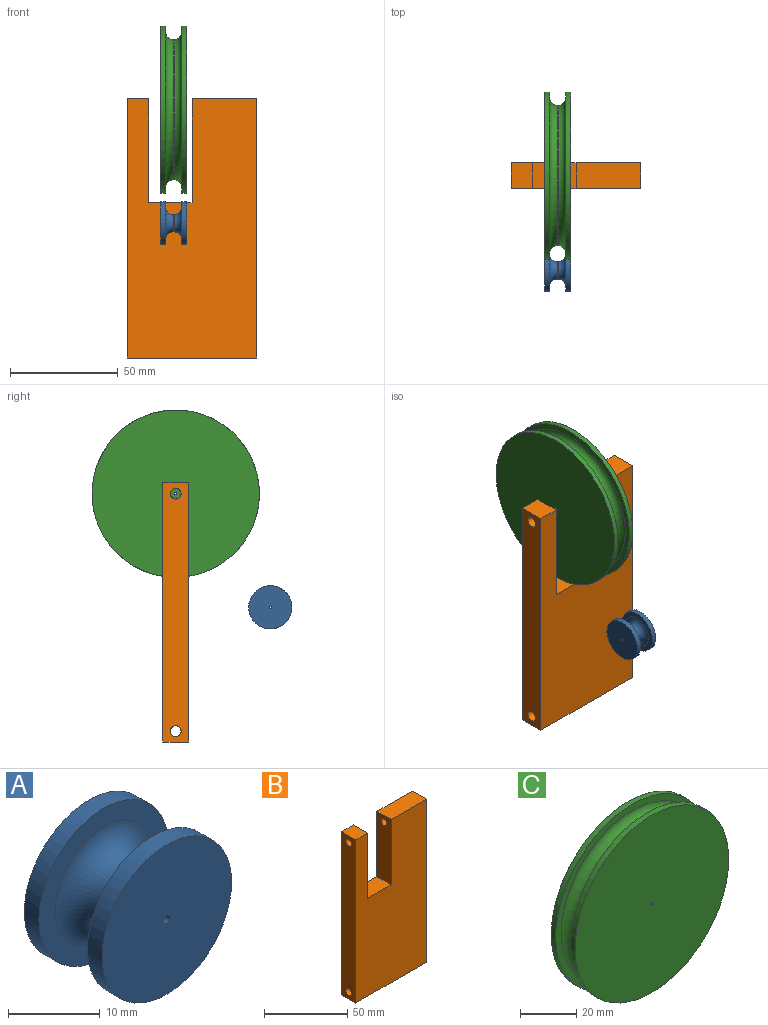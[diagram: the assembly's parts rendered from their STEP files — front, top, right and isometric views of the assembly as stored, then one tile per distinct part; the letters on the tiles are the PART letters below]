
ASSEMBLY  parts=3 mates=3
PART A: 10 faces, bbox 21.6x12x21.6 mm
  f0: cylinder r=10mm len=20mm, axis (0,1,0), area 141.4mm2, adj f1,f5
  f1: plane 20x20mm, normal (0,1,0), area 313.4mm2, adj f0,f9
  f2: torus R=7.5mm, axis (0,-1,0), area 182.1mm2, adj f3,f6
  f3: cylinder r=4mm len=8mm, axis (0,-1,0), area 12.6mm2, adj f2,f4
  f4: torus R=7.5mm, axis (0,-1,0), area 182.1mm2, adj f3,f5
  f5: plane 20x20mm, normal (0,-1,0), area 137.4mm2, adj f0,f4
  f6: plane 20x20mm, normal (0,1,0), area 137.4mm2, adj f2,f8
  f7: plane 20x20mm, normal (0,-1,0), area 313.4mm2, adj f8,f9
  f8: cylinder r=10mm len=20mm, axis (0,1,0), area 141.4mm2, adj f6,f7
  f9: cylinder r=0.5mm len=12mm, axis (0,1,0), area 37.7mm2, adj f1,f7
PART B: 13 faces, bbox 60x12x120 mm
  f0: plane 30x12mm, normal (0,0,1), area 360mm2, adj f1,f2,f3,f7
  f1: plane 120x60mm, normal (0,-1,0), area 6240mm2, adj f0,f3,f4,f5,f6,f7,f8,f9
  f2: plane 120x60mm, normal (0,1,0), area 6240mm2, adj f0,f3,f4,f5,f6,f7,f8,f9
  f3: plane 120x12mm, normal (1,0,0), area 1400.7mm2, adj f0,f1,f2,f6,f11,f12
  f4: plane 12x10mm, normal (0,0,1), area 120mm2, adj f1,f2,f5,f9
  f5: plane 120x12mm, normal (-1,0,0), area 1400.7mm2, adj f1,f2,f4,f6,f10,f12
  f6: plane 60x12mm, normal (0,0,-1), area 720mm2, adj f1,f2,f3,f5
  f7: plane 48x12mm, normal (-1,0,0), area 556.4mm2, adj f0,f1,f2,f8,f11
  f8: plane 20x12mm, normal (0,0,1), area 240mm2, adj f1,f2,f7,f9
  f9: plane 48x12mm, normal (1,0,0), area 556.4mm2, adj f1,f2,f4,f8,f10
  f10: cylinder r=2.5mm len=10mm, axis (1,0,0), area 157.1mm2, adj f5,f9
  f11: cylinder r=2.5mm len=30mm, axis (1,0,0), area 471.2mm2, adj f3,f7
  f12: cylinder r=2.5mm len=60mm, axis (1,0,0), area 942.5mm2, adj f3,f5
PART C: 10 faces, bbox 83.3x12x83.3 mm
  f0: cylinder r=38.75mm len=77.5mm, axis (0,1,0), area 547.8mm2, adj f1,f2
  f1: plane 77.5x77.5mm, normal (0,1,0), area 4716.5mm2, adj f0,f9
  f2: plane 77.5x77.5mm, normal (0,-1,0), area 645.8mm2, adj f0,f5
  f3: plane 77.5x77.5mm, normal (0,1,0), area 645.8mm2, adj f6,f8
  f4: cylinder r=32.5mm len=65mm, axis (0,-1,0), area 102.1mm2, adj f5,f6
  f5: torus R=36mm, axis (0,-1,0), area 1166.6mm2, adj f2,f4
  f6: torus R=36mm, axis (0,-1,0), area 1166.6mm2, adj f3,f4
  f7: plane 77.5x77.5mm, normal (0,-1,0), area 4716.5mm2, adj f8,f9
  f8: cylinder r=38.75mm len=77.5mm, axis (0,1,0), area 547.8mm2, adj f3,f7
  f9: cylinder r=0.5mm len=12mm, axis (0,1,0), area 37.7mm2, adj f1,f7
PLACE A rot(axis=(-0.27,0.27,0.92),94.6deg) t=(-8.5,-49.81,2.37)mm
PLACE B at identity fixed
PLACE C rot(axis=(0.66,-0.66,0.34),142.2deg) t=(-8.5,-6,55)mm
MATE planar C.f0 <-> A.f0  axis (1,0,0) through (-2.5,-6,55)mm
MATE parallel C.f0 <-> B.f3  axis (1,0,0) through (-2.5,-6,55)mm
MATE revolute C.f0 <-> B.f10  axis (1,0,0) through (-2.5,-6,55)mm
